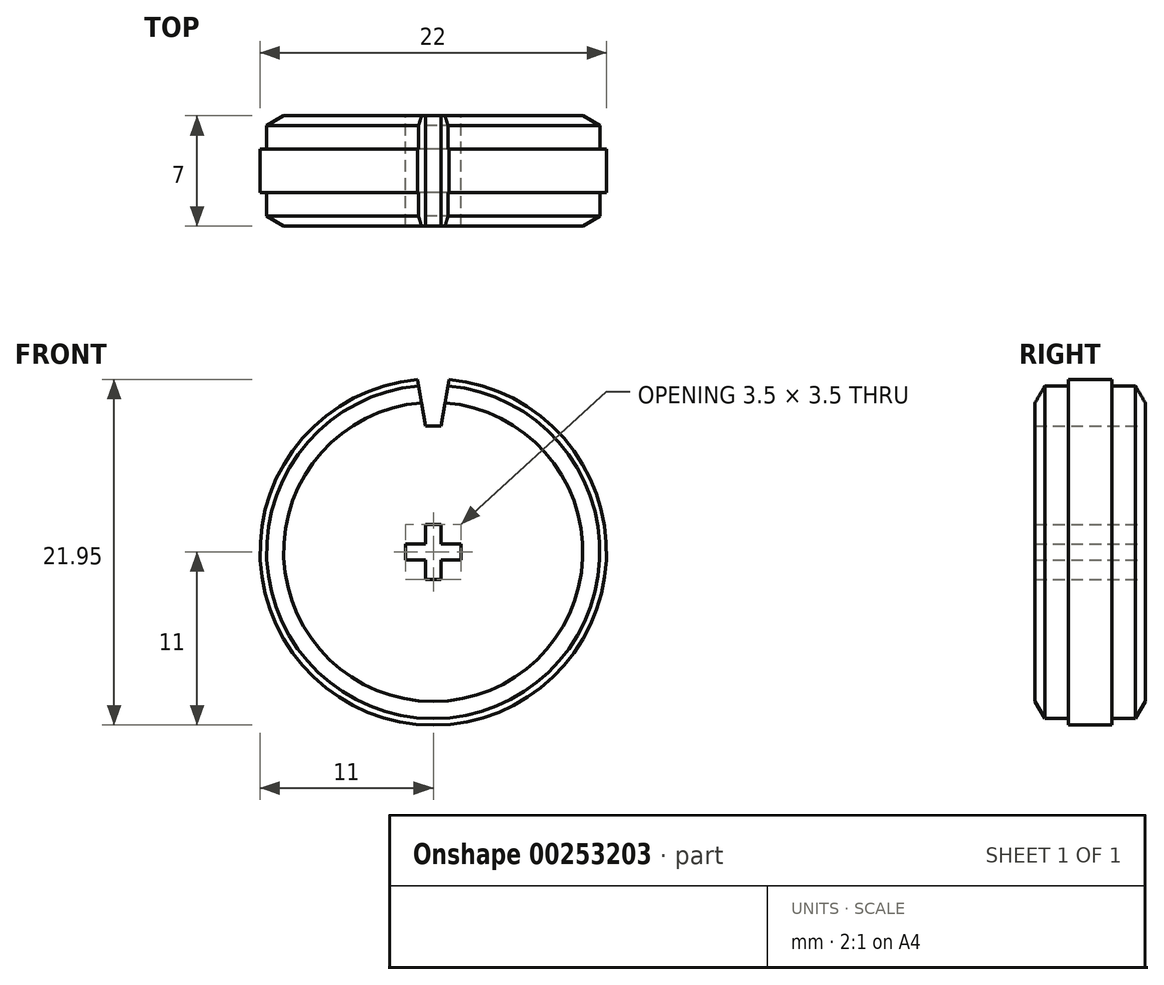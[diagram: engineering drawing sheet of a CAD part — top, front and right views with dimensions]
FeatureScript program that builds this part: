
annotation { "Feature Type Name" : "Feature", "Feature Type Description" : "" }
export const myFeature = defineFeature(function(context is Context, id is Id, definition is map)
    precondition{}
    {
        {
            var Q0;
            Q0=qCreatedBy(makeId("Front.planeOp"),FACE);
            var sketch = newSketch(context, id + "F0", { "sketchPlane" : qUnion([Q0])});
            skCircle(sketch, "E0", {"center": v(0, 0) * mm, "radius": 11 * mm});
            skLineSegment(sketch, "E1.0", {"start": v(-0.5, 0.5) * mm, "end": v(-0.5, 1.75) * mm});
            skLineSegment(sketch, "E1.1", {"start": v(-0.5, 1.75) * mm, "end": v(0.5, 1.75) * mm});
            skLineSegment(sketch, "E1.2", {"start": v(0.5, 1.75) * mm, "end": v(0.5, 0.5) * mm});
            skLineSegment(sketch, "E1.3", {"start": v(0.5, 0.5) * mm, "end": v(1.75, 0.5) * mm});
            skLineSegment(sketch, "E1.4", {"start": v(1.75, 0.5) * mm, "end": v(1.75, -0.5) * mm});
            skLineSegment(sketch, "E1.5", {"start": v(1.75, -0.5) * mm, "end": v(0.5, -0.5) * mm});
            skLineSegment(sketch, "E1.6", {"start": v(0.5, -0.5) * mm, "end": v(0.5, -1.75) * mm});
            skLineSegment(sketch, "E1.7", {"start": v(0.5, -1.75) * mm, "end": v(-0.5, -1.75) * mm});
            skLineSegment(sketch, "E1.8", {"start": v(-0.5, -1.75) * mm, "end": v(-0.5, -0.5) * mm});
            skLineSegment(sketch, "E1.9", {"start": v(-0.5, -0.5) * mm, "end": v(-1.75, -0.5) * mm});
            skLineSegment(sketch, "E1.10", {"start": v(-1.75, -0.5) * mm, "end": v(-1.75, 0.5) * mm});
            skLineSegment(sketch, "E1.11", {"start": v(-1.75, 0.5) * mm, "end": v(-0.5, 0.5) * mm});
            skLineSegment(sketch, "E2", {"start": v(-0.5, 0.5) * mm, "end": v(0.5, -0.5) * mm, "construction": true});
            skLineSegment(sketch, "E3", {"start": v(-0.5, -0.5) * mm, "end": v(0.5, 0.5) * mm, "construction": true});
            skSolve(sketch);
        }
        {
            var Q0;
            Q0=qSketchRegion(id+"F0",true);
            extrude(context, id + "F1", {"entities" : qUnion([Q0]), "depth" : 7 * mm});
        }
        {
            var Q0;
            Q0=qCreatedBy(makeId("Right.planeOp"),FACE);
            var sketch = newSketch(context, id + "F2", { "sketchPlane" : qUnion([Q0])});
            skLineSegment(sketch, "E4", {"start": v(0, 0) * mm, "end": v(5.2, 0) * mm, "construction": true});
            skLineSegment(sketch, "E5", {"start": v(-7, 9.5) * mm, "end": v(-6.38, 10.58) * mm});
            skLineSegment(sketch, "E6", {"start": v(-6.38, 10.58) * mm, "end": v(-4.88, 10.58) * mm});
            skLineSegment(sketch, "E7", {"start": v(-4.88, 10.58) * mm, "end": v(-4.88, 11) * mm});
            skLineSegment(sketch, "E8", {"start": v(-4.87, 11) * mm, "end": v(-2.12, 11) * mm});
            skLineSegment(sketch, "E9", {"start": v(-2.12, 11) * mm, "end": v(-2.12, 10.58) * mm});
            skLineSegment(sketch, "E10", {"start": v(-2.12, 10.58) * mm, "end": v(-0.63, 10.58) * mm});
            skLineSegment(sketch, "E11", {"start": v(-0.63, 10.58) * mm, "end": v(0, 9.5) * mm});
            skLineSegment(sketch, "E12", {"start": v(0, 9.5) * mm, "end": v(0, 12.5) * mm});
            skLineSegment(sketch, "E13", {"start": v(0, 12.5) * mm, "end": v(-7, 12.5) * mm});
            skLineSegment(sketch, "E14", {"start": v(-7, 12.5) * mm, "end": v(-7, 9.5) * mm});
            skPoint(sketch, "E15", {"position": v(0, 11) * mm});
            skPoint(sketch, "E16.positionSnap0", {"position": v(-7, 11) * mm});
            skSolve(sketch);
        }
        {
            var Q0;
            Q0=qSketchRegion(id+"F2",true);
            var Q1;
            Q1=sQuery(id+"F2.wireOp",EDGE,"E4");
            revolve(context, id + "F3", {"operationType" : NewBodyOperationType.REMOVE, "entities" : qUnion([Q0]), "axis" : qUnion([Q1]), "revolveType" : RevolveType.FULL, "oppositeDirection" : true});
        }
        {
            var Q0;
            Q0=qCreatedBy(makeId("Front.planeOp"),FACE);
            var sketch = newSketch(context, id + "F4", { "sketchPlane" : qUnion([Q0])});
            skLineSegment(sketch, "E17", {"start": v(1, 10.95) * mm, "end": v(0.5, 7.98) * mm});
            skArc(sketch, "E18", {"start": v(0.5, 7.98) * mm, "mid": v(0, 8) * mm, "end": v(-0.5, 7.98) * mm});
            skLineSegment(sketch, "E19", {"start": v(-0.5, 7.98) * mm, "end": v(-1, 10.95) * mm});
            skArc(sketch, "E20", {"start": v(1, 10.95) * mm, "mid": v(0, 11) * mm, "end": v(-1, 10.95) * mm});
            skPoint(sketch, "E21", {"position": v(0, 11) * mm});
            skPoint(sketch, "E21.positionSnap0", {"position": v(0, 11) * mm});
            skPoint(sketch, "E22", {"position": v(0, 8) * mm});
            skSolve(sketch);
        }
        {
            var Q0;
            Q0=qSketchRegion(id+"F4",true);
            extrude(context, id + "F5", {"entities" : qUnion([Q0]), "operationType" : NewBodyOperationType.REMOVE, "endBound" : BoundingType.THROUGH_ALL, "depth" : 25 * mm});
        }
    });
